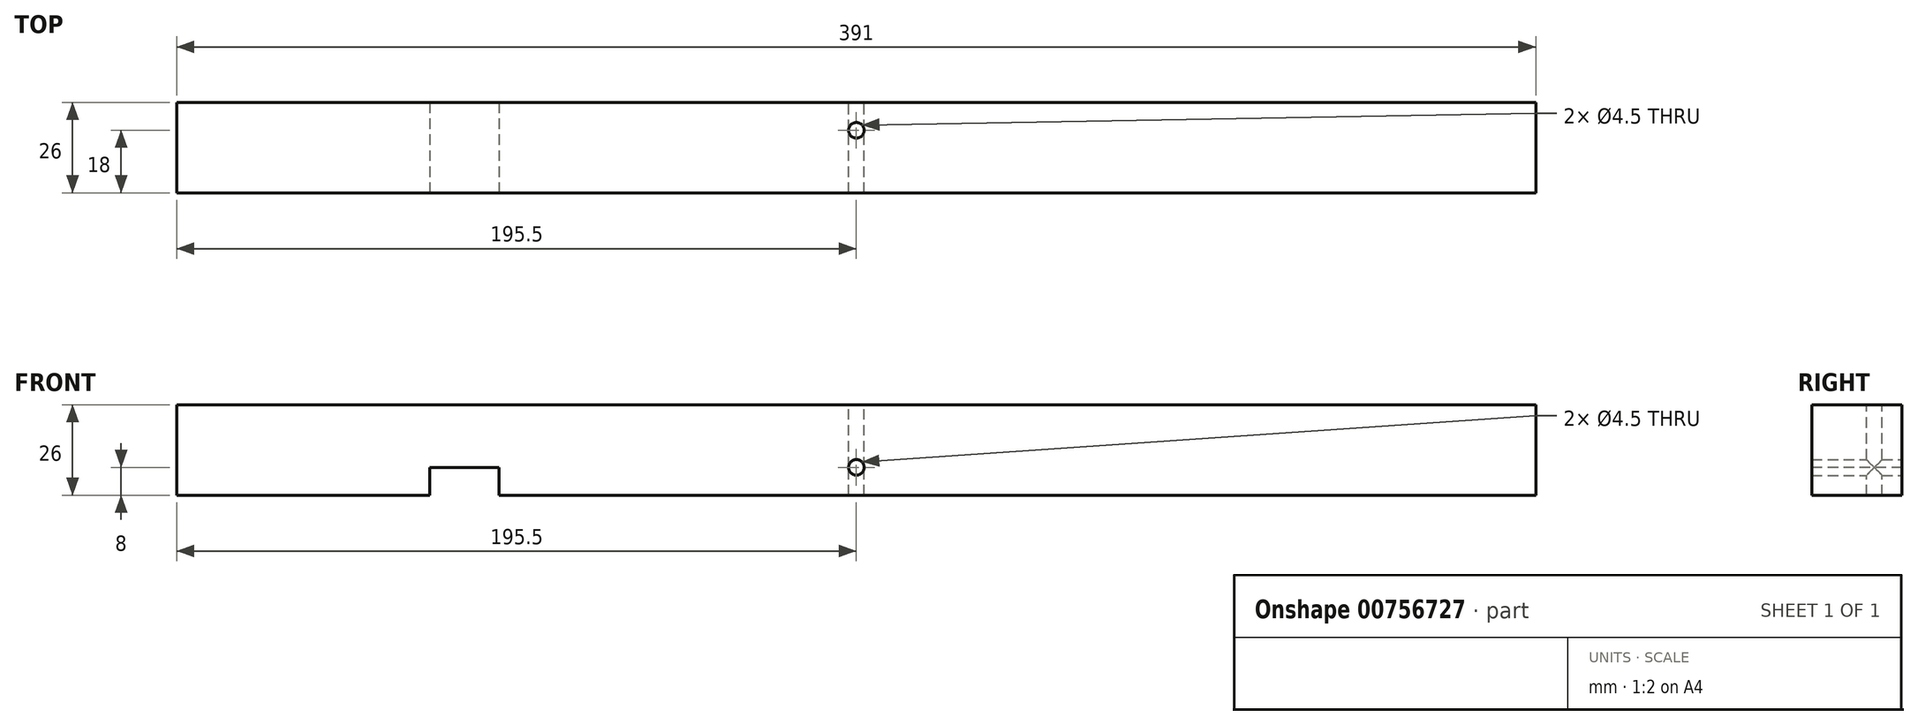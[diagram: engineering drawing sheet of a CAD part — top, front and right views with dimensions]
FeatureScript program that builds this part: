
annotation { "Feature Type Name" : "Feature", "Feature Type Description" : "" }
export const myFeature = defineFeature(function(context is Context, id is Id, definition is map)
    precondition{}
    {
        {
            var Q0;
            Q0=qCreatedBy(makeId("Right.planeOp"),FACE);
            var sketch = newSketch(context, id + "F0", { "sketchPlane" : qUnion([Q0])});
            skLineSegment(sketch, "E0.bottom", {"start": v(-13, 26) * mm, "end": v(13, 26) * mm});
            skLineSegment(sketch, "E0.top", {"start": v(-13, 0) * mm, "end": v(13, 0) * mm});
            skLineSegment(sketch, "E0.left", {"start": v(-13, 26) * mm, "end": v(-13, 0) * mm});
            skLineSegment(sketch, "E0.right", {"start": v(13, 26) * mm, "end": v(13, 0) * mm});
            skSolve(sketch);
        }
        {
            var Q0;
            Q0=makeQuery(id+"F0.imprint","IMPRINT",FACE,{"disambiguationData":[TD([[makeQuery(id+"F0.imprint","IMPRINT",EDGE,{"derivedFrom":sQuery(id+"F0.wireOp",EDGE,"E0.bottom")}),-1.0]])]});
            extrude(context, id + "F1", {"entities" : qUnion([Q0]), "depth" : 391 * mm, "offsetDistance" : 25 * mm, "symmetric" : true});
        }
        {
            var Q0;
            Q0=makeQuery(id+"F1.opExtrude","SWEPT_FACE",FACE,{"disambiguationData":[OSD([sQuery(id+"F0.wireOp",EDGE,"E0.bottom")])]});
            var sketch = newSketch(context, id + "F2", { "sketchPlane" : qUnion([Q0])});
            skLineSegment(sketch, "E1.bottom", {"start": v(-6, -8) * mm, "end": v(6, -8) * mm});
            skLineSegment(sketch, "E1.top", {"start": v(-6, -13) * mm, "end": v(6, -13) * mm});
            skLineSegment(sketch, "E1.left", {"start": v(-6, -8) * mm, "end": v(-6, -13) * mm});
            skLineSegment(sketch, "E1.right", {"start": v(6, -8) * mm, "end": v(6, -13) * mm});
            skSolve(sketch);
        }
        {
            var Q0;
            Q0=makeQuery(id+"F1.opExtrude","SWEPT_FACE",FACE,{"disambiguationData":[OSD([sQuery(id+"F0.wireOp",EDGE,"E0.left")])]});
            var sketch = newSketch(context, id + "F3", { "sketchPlane" : qUnion([Q0])});
            skPoint(sketch, "E2", {"position": v(0, 8) * mm});
            skSolve(sketch);
        }
        {
            var Q0;
            Q0=sQuery(id+"F3.wireOp",VERTEX,"E2");
            var Q1;
            Q1=makeQuery(id+"F1.opExtrude","SWEPT_BODY",BODY,{"disambiguationData":[OSD([sQuery(id+"F0.wireOp",EDGE,"E0.bottom"),sQuery(id+"F0.wireOp",EDGE,"E0.top"),sQuery(id+"F0.wireOp",EDGE,"E0.left"),sQuery(id+"F0.wireOp",EDGE,"E0.right")])]});
            hole(context, id + "F4", {"style" : HoleStyle.SIMPLE, "endStyle" : HoleEndStyle.THROUGH, "holeDiameter" : 4.5 * mm, "majorDiameter" : 5 * mm, "isTappedThrough" : true, "tappedDepth" : 12 * mm, "tapClearance" : 3, "locations" : qUnion([Q0]), "scope" : qUnion([Q1])});
        }
        {
            var Q0;
            Q0=makeQuery(id+"F1.opExtrude","SWEPT_FACE",FACE,{"disambiguationData":[OSD([sQuery(id+"F0.wireOp",EDGE,"E0.top")])]});
            var sketch = newSketch(context, id + "F5", { "sketchPlane" : qUnion([Q0])});
            skPoint(sketch, "E3", {"position": v(0, -5) * mm});
            skSolve(sketch);
        }
        {
            var Q0;
            Q0=sQuery(id+"F5.wireOp",VERTEX,"E3");
            var Q1;
            Q1=makeQuery(id+"F1.opExtrude","SWEPT_BODY",BODY,{"disambiguationData":[OSD([sQuery(id+"F0.wireOp",EDGE,"E0.bottom"),sQuery(id+"F0.wireOp",EDGE,"E0.top"),sQuery(id+"F0.wireOp",EDGE,"E0.left"),sQuery(id+"F0.wireOp",EDGE,"E0.right")])]});
            hole(context, id + "F6", {"style" : HoleStyle.SIMPLE, "endStyle" : HoleEndStyle.THROUGH, "holeDiameter" : 4.5 * mm, "majorDiameter" : 5 * mm, "isTappedThrough" : true, "tappedDepth" : 12 * mm, "tapClearance" : 3, "locations" : qUnion([Q0]), "scope" : qUnion([Q1])});
        }
        {
            var Q0;
            Q0=makeQuery(id+"F1.opExtrude","SWEPT_FACE",FACE,{"disambiguationData":[OSD([sQuery(id+"F0.wireOp",EDGE,"E0.left")])]});
            var sketch = newSketch(context, id + "F7", { "sketchPlane" : qUnion([Q0])});
            skLineSegment(sketch, "E4.bottom", {"start": v(-122.75, 0) * mm, "end": v(-102.75, 0) * mm});
            skLineSegment(sketch, "E4.top", {"start": v(-122.75, 8) * mm, "end": v(-102.75, 8) * mm});
            skLineSegment(sketch, "E4.left", {"start": v(-122.75, 0) * mm, "end": v(-122.75, 8) * mm});
            skLineSegment(sketch, "E4.right", {"start": v(-102.75, 0) * mm, "end": v(-102.75, 8) * mm});
            skSolve(sketch);
        }
        {
            var Q0;
            Q0 = qSketchRegion(id + "F7", true);
            extrude(context, id + "F8", {"entities" : qUnion([Q0]), "operationType" : NewBodyOperationType.REMOVE, "endBound" : BoundingType.UP_TO_NEXT, "oppositeDirection" : true, "depth" : 25 * mm, "offsetDistance" : 25 * mm});
        }
    });
